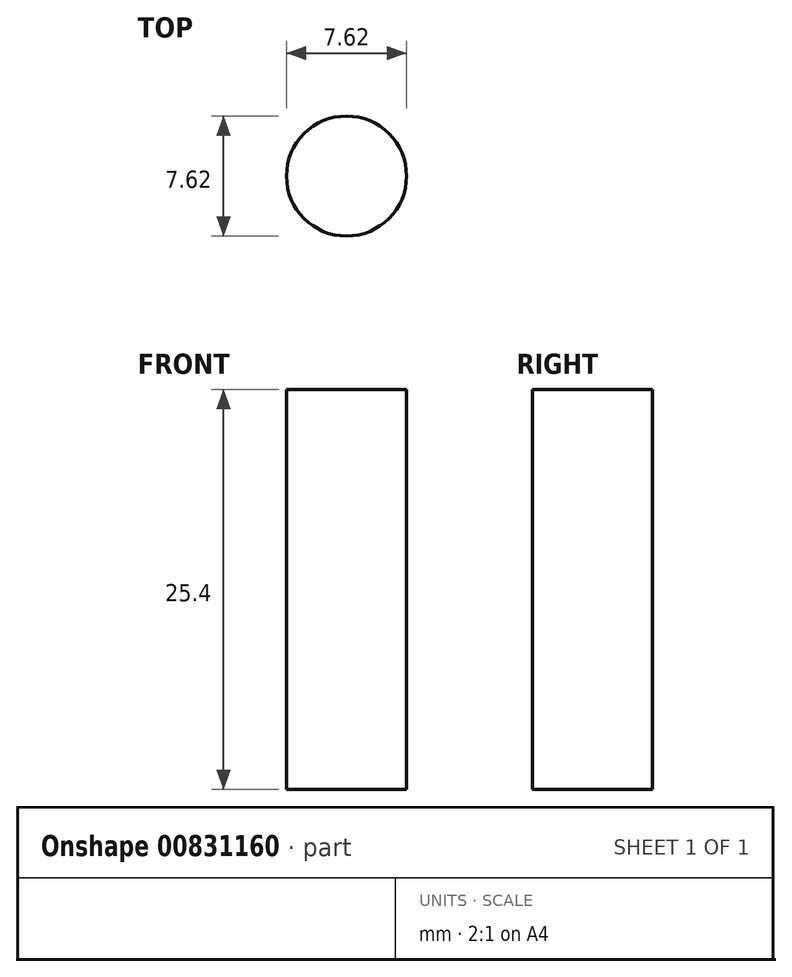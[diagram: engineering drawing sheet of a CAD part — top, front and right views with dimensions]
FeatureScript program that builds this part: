
annotation { "Feature Type Name" : "Feature", "Feature Type Description" : "" }
export const myFeature = defineFeature(function(context is Context, id is Id, definition is map)
    precondition{}
    {
        {
            var Q0;
            Q0=qCreatedBy(makeId("Front.planeOp"),FACE);
            var sketch = newSketch(context, id + "F0", { "sketchPlane" : qUnion([Q0])});
            skLineSegment(sketch, "E0.bottom", {"start": v(0, 0) * mm, "end": v(3.81, 0) * mm});
            skLineSegment(sketch, "E0.top", {"start": v(0, 25.4) * mm, "end": v(3.8, 25.4) * mm});
            skLineSegment(sketch, "E0.left", {"start": v(0, 0) * mm, "end": v(0, 25.4) * mm});
            skLineSegment(sketch, "E0.right", {"start": v(3.81, 0) * mm, "end": v(3.8, 25.4) * mm});
            skPoint(sketch, "E1.left.start.orphan", {"position": v(-27.4, 25.4) * mm});
            skPoint(sketch, "E1.top.end.orphan", {"position": v(-23.6, 0) * mm});
            skPoint(sketch, "E2.top.end.orphan", {"position": v(-11.75, 0) * mm});
            skPoint(sketch, "E2.bottom.end.orphan", {"position": v(-11.75, 25.4) * mm});
            skPoint(sketch, "E2.bottom.start.orphan", {"position": v(-15.56, 25.4) * mm});
            skPoint(sketch, "E3.top.end.orphan", {"position": v(11.73, 25.4) * mm});
            skPoint(sketch, "E3.bottom.start.orphan", {"position": v(7.92, 0) * mm});
            skPoint(sketch, "E4.left.start.orphan", {"position": v(19.76, 0) * mm});
            skPoint(sketch, "E4.right.end.orphan", {"position": v(23.57, 25.4) * mm});
            skPoint(sketch, "E5.top.end.orphan", {"position": v(38.29, 0) * mm});
            skSolve(sketch);
        }
        {
            var Q0;
            Q0 = qSketchRegion(id + "F0", true);
            var Q1;
            Q1=sQuery(id+"F0.wireOp",EDGE,"E0.left");
            revolve(context, id + "F1", {"surfaceOperationType" : NewSurfaceOperationType.NEW, "entities" : qUnion([Q0]), "axis" : qUnion([Q1]), "revolveType" : RevolveType.FULL});
        }
    });
